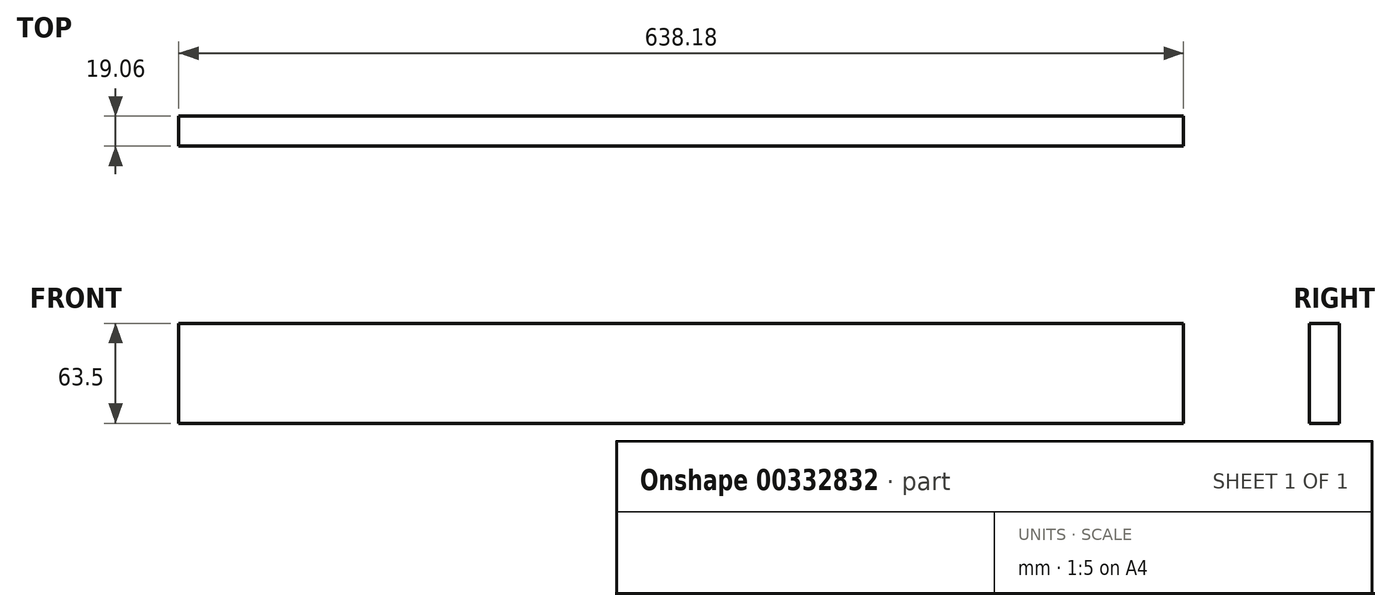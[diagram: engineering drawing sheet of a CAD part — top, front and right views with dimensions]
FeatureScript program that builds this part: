
annotation { "Feature Type Name" : "Feature", "Feature Type Description" : "" }
export const myFeature = defineFeature(function(context is Context, id is Id, definition is map)
    precondition{}
    {
        {
            var Q0;
            Q0=qCreatedBy(makeId("Front.planeOp"),FACE);
            var sketch = newSketch(context, id + "F0", { "sketchPlane" : qUnion([Q0])});
            skLineSegment(sketch, "E0.bottom", {"start": v(554.04, 31.75) * mm, "end": v(-84.14, 31.75) * mm});
            skLineSegment(sketch, "E0.top", {"start": v(554.04, -31.75) * mm, "end": v(-84.14, -31.75) * mm});
            skLineSegment(sketch, "E0.left", {"start": v(554.04, 31.75) * mm, "end": v(554.04, -31.75) * mm});
            skPoint(sketch, "E0.middle", {"position": v(0, 0) * mm});
            skPoint(sketch, "E0.right.start.orphan", {"position": v(-554.04, 31.75) * mm});
            skPoint(sketch, "E1.orphan", {"position": v(-554.04, -31.75) * mm});
            skLineSegment(sketch, "E2", {"start": v(-84.14, 31.75) * mm, "end": v(-84.14, -31.75) * mm});
            skPoint(sketch, "E3.end.orphan", {"position": v(-490.54, -31.75) * mm});
            skSolve(sketch);
        }
        {
            var Q0;
            Q0=makeQuery(id+"F0.imprint","IMPRINT",FACE,{"disambiguationData":[TD([[makeQuery(id+"F0.imprint","IMPRINT",EDGE,{"derivedFrom":sQuery(id+"F0.wireOp",EDGE,"E0.bottom")}),1.0]])]});
            extrude(context, id + "F1", {"entities" : qUnion([Q0]), "endBound" : BoundingType.SYMMETRIC, "depth" : 19.05 * mm});
        }
    });
